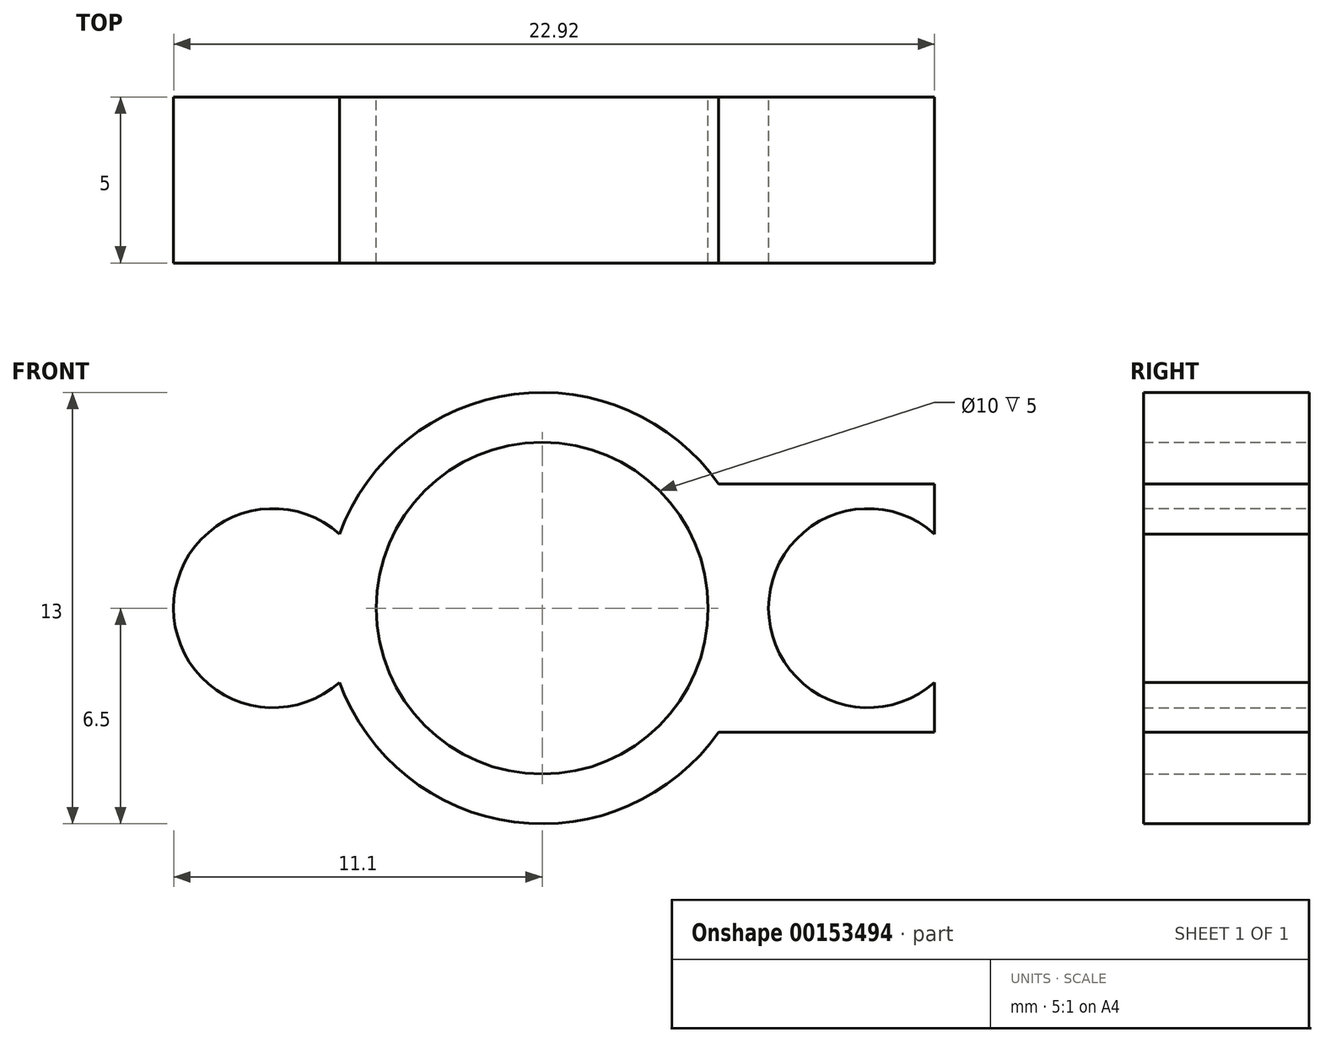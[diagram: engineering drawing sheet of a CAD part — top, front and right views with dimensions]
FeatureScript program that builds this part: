
annotation { "Feature Type Name" : "Feature", "Feature Type Description" : "" }
export const myFeature = defineFeature(function(context is Context, id is Id, definition is map)
    precondition{}
    {
        {
            var Q0;
            Q0=qCreatedBy(makeId("Front.planeOp"),FACE);
            var sketch = newSketch(context, id + "F0", { "sketchPlane" : qUnion([Q0])});
            skCircle(sketch, "E0", {"center": v(0, 0) * mm, "radius": 6.5 * mm});
            skArc(sketch, "E1", {"start": v(-6.1, 2.24) * mm, "mid": v(-11.1, 0) * mm, "end": v(-6.1, -2.24) * mm});
            skLineSegment(sketch, "E2", {"start": v(5.32, 3.74) * mm, "end": v(11.82, 3.74) * mm});
            skLineSegment(sketch, "E3", {"start": v(11.82, 3.74) * mm, "end": v(11.82, 2.24) * mm});
            skLineSegment(sketch, "E4", {"start": v(5.32, -3.74) * mm, "end": v(11.82, -3.74) * mm});
            skLineSegment(sketch, "E5", {"start": v(11.82, -3.74) * mm, "end": v(11.82, -2.24) * mm});
            skArc(sketch, "E6", {"start": v(11.82, 2.24) * mm, "mid": v(6.82, 0) * mm, "end": v(11.82, -2.24) * mm});
            skCircle(sketch, "E7", {"center": v(0, 0) * mm, "radius": 5 * mm});
            skSolve(sketch);
        }
        {
            var Q0;
            Q0=makeQuery(id+"F0.imprint","IMPRINT",FACE,{"disambiguationData":[TD([[makeQuery(id+"F0.imprint","IMPRINT",EDGE,{"derivedFrom":sQuery(id+"F0.wireOp",EDGE,"E7")}),-1.0]])]});
            var Q1;
            Q1=makeQuery(id+"F0.imprint","IMPRINT",FACE,{"disambiguationData":[TD([[makeQuery(id+"F0.imprint","IMPRINT",EDGE,{"derivedFrom":sQuery(id+"F0.wireOp",EDGE,"E1")}),1.0]])]});
            var Q2;
            {var subQ1=sQuery(id+"F0.wireOp",EDGE,"E2");Q2=makeQuery(id+"F0.imprint","IMPRINT",FACE,{"disambiguationData":[TD([[makeQuery(id+"F0.imprint","IMPRINT",EDGE,{"derivedFrom":subQ1}),-1.0]])]});}
            extrude(context, id + "F1", {"entities" : qUnion([Q0, Q1, Q2]), "depth" : 5 * mm});
        }
    });
